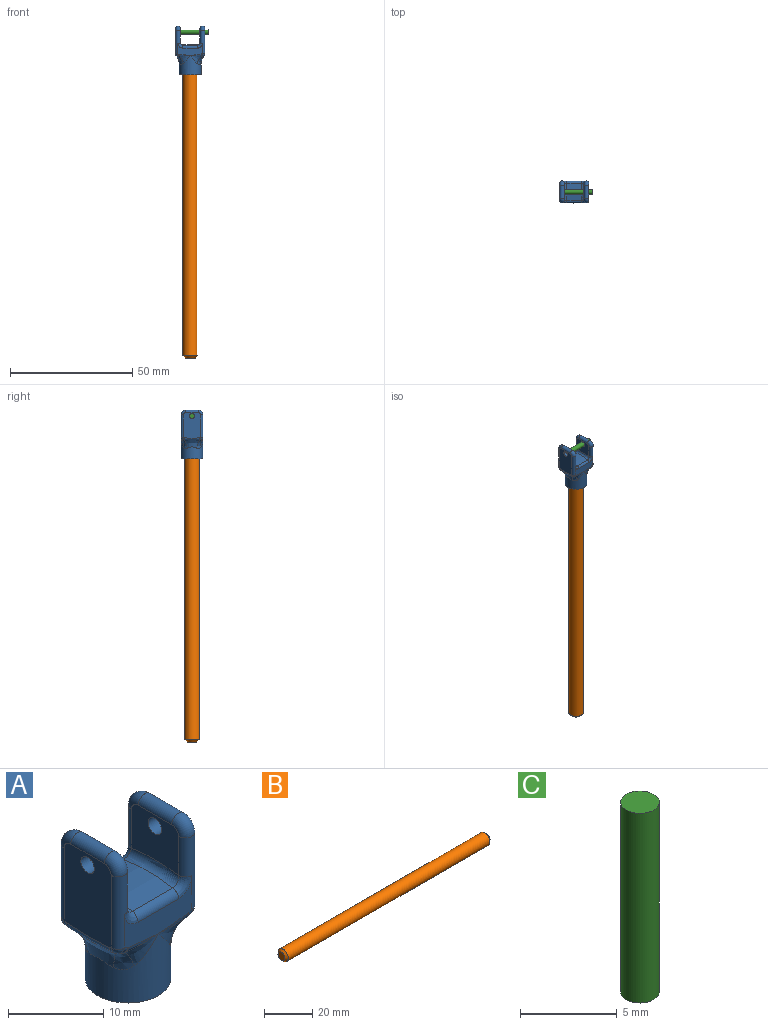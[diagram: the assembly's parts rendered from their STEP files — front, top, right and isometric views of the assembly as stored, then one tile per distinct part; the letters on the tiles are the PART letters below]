
ASSEMBLY  parts=3 mates=1
PART A: 63 faces, bbox 12.4x9.7x20.5 mm
  f0: plane 10.37x5.36mm, normal (0,1,0), area 29.1mm2, adj f12,f14,f38,f39,f40,f41,f42,f43
  f1: plane 10.33x5.33mm, normal (0,-1,0), area 29.1mm2, adj f8,f13,f30,f31,f32,f49,f50,f51
  f2: plane 7x6mm, normal (-1,0,0), area 37.2mm2, adj f8,f9,f10,f11,f12,f28,f54
  f3: cylinder r=4.5mm len=9mm, axis (0,0,-1), area 148.7mm2, adj f18,f19,f20,f21,f22,f23,f24,f25
  f4: plane 7x6mm, normal (1,0,0), area 37.2mm2, adj f13,f14,f15,f16,f17,f29,f57
  f5: plane 10.55x7mm, normal (-1,0,0), area 69.9mm2, adj f13,f14,f15,f16,f17,f29,f34,f35
  f6: plane 10.55x7mm, normal (1,0,0), area 69.9mm2, adj f8,f9,f10,f11,f12,f28,f45,f46
  f7: cylinder r=21.21mm len=7.35mm, axis (-1,0,0), area 44.3mm2, adj f53,f54,f57,f58
  f8: cylinder r=1mm len=9.36mm, axis (0,0,1), area 22.6mm2, adj f1,f2,f6,f9,f48,f56
  f9: torus R=1mm, axis (-1,0,0), area 8.1mm2, adj f2,f6,f8,f10
  f10: cylinder r=1mm len=5mm, axis (0,-1,0), area 15.7mm2, adj f2,f6,f9,f11
  f11: torus R=1mm, axis (-1,0,0), area 8.1mm2, adj f2,f6,f10,f12
  f12: cylinder r=1mm len=9.36mm, axis (0,0,-1), area 22.6mm2, adj f0,f2,f6,f11,f44,f52
  f13: cylinder r=1mm len=9.36mm, axis (0,0,-1), area 22.6mm2, adj f1,f4,f5,f15,f33,f59
  f14: cylinder r=1mm len=9.36mm, axis (0,0,1), area 22.6mm2, adj f0,f4,f5,f16,f37,f55
  f15: torus R=1mm, axis (-1,0,0), area 8.1mm2, adj f4,f5,f13,f17
  f16: torus R=1mm, axis (-1,0,0), area 8.1mm2, adj f4,f5,f14,f17
  f17: cylinder r=1mm len=5mm, axis (0,1,0), area 15.7mm2, adj f4,f5,f15,f16
  f18: bspline ~5.51x3.49mm, area 4.6mm2, adj f3,f19,f41
  f19: bspline ~3.75x3.7mm, area 6.7mm2, adj f3,f18,f20,f42,f43,f45
  f20: bspline ~8.76x3.84mm, area 17mm2, adj f3,f19,f21,f46
  f21: bspline ~3.75x3.6mm, area 6.7mm2, adj f3,f20,f22,f47,f49,f50
  f22: bspline ~5.51x3.49mm, area 4.6mm2, adj f3,f21,f51
  f23: bspline ~5.51x3.49mm, area 4.6mm2, adj f3,f24,f30
  f24: bspline ~3.75x3.7mm, area 6.7mm2, adj f3,f23,f25,f31,f32,f34
  f25: bspline ~8.76x3.84mm, area 17mm2, adj f3,f24,f26,f35
  f26: bspline ~3.75x3.6mm, area 6.7mm2, adj f3,f25,f27,f36,f38,f39
  f27: bspline ~5.51x3.49mm, area 4.6mm2, adj f3,f26,f40
  f28: cylinder r=1mm len=2mm, axis (1,0,0), area 12.6mm2, adj f2,f6
  f29: cylinder r=1mm len=2mm, axis (1,0,0), area 12.6mm2, adj f4,f5
  f30: bspline ~4.78x0.76mm, area 1.2mm2, adj f1,f23,f31
  f31: bspline ~0.8x0.45mm, area 0.1mm2, adj f1,f24,f30,f32
  f32: bspline ~1.15x1.11mm, area 0.7mm2, adj f1,f24,f31,f33
  f33: sphere r=1mm, area 1.1mm2, adj f13,f32,f34
  f34: bspline ~0.98x0.87mm, area 0.5mm2, adj f5,f24,f33,f35
  f35: bspline ~6.85x0.85mm, area 5.5mm2, adj f5,f25,f34,f36
  f36: bspline ~0.97x0.85mm, area 0.5mm2, adj f5,f26,f35,f37
  f37: sphere r=1mm, area 1.1mm2, adj f14,f36,f38
  f38: bspline ~1.2x1.14mm, area 0.7mm2, adj f0,f26,f37,f39
  f39: bspline ~0.79x0.44mm, area 0.1mm2, adj f0,f26,f38,f40
  f40: bspline ~4.9x0.78mm, area 1.2mm2, adj f0,f27,f39
  f41: bspline ~4.69x0.74mm, area 1.2mm2, adj f0,f18,f42
  f42: bspline ~0.8x0.45mm, area 0.1mm2, adj f0,f19,f41,f43
  f43: bspline ~1.31x1.18mm, area 0.7mm2, adj f0,f19,f42,f44
  f44: sphere r=1mm, area 1mm2, adj f12,f43,f45
  f45: bspline ~0.98x0.85mm, area 0.5mm2, adj f6,f19,f44,f46
  f46: bspline ~7.61x0.93mm, area 5.5mm2, adj f6,f20,f45,f47
  f47: bspline ~0.98x0.85mm, area 0.5mm2, adj f6,f21,f46,f48
  f48: sphere r=1mm, area 1mm2, adj f8,f47,f49
  f49: bspline ~1.2x1.14mm, area 0.7mm2, adj f1,f21,f48,f50
  f50: bspline ~0.8x0.44mm, area 0.1mm2, adj f1,f21,f49,f51
  f51: bspline ~4.69x0.74mm, area 1.2mm2, adj f1,f22,f50
  f52: bspline ~2.44x2.36mm, area 3.2mm2, adj f0,f12,f53,f54
  f53: cylinder r=1mm len=6mm, axis (-1,0,0), area 8.4mm2, adj f0,f7,f52,f55
  f54: torus R=22.21mm, axis (-1,0,0), area 11.3mm2, adj f2,f7,f52,f56
  f55: bspline ~2.49x2.36mm, area 3.2mm2, adj f0,f14,f53,f57
  f56: bspline ~2.49x2.36mm, area 3.2mm2, adj f1,f8,f54,f58
  f57: torus R=22.21mm, axis (-1,0,0), area 11.3mm2, adj f4,f7,f55,f59
  f58: cylinder r=1mm len=6mm, axis (-1,0,0), area 8.4mm2, adj f1,f7,f56,f59
  f59: bspline ~2.44x2.36mm, area 3.2mm2, adj f1,f13,f57,f58
  f60: plane 9x9mm, normal (0,0,-1), area 32.9mm2, adj f3,f62
  f61: plane 6.25x6.25mm, normal (0,0,-1), area 30.7mm2, adj f62
  f62: cylinder r=3.12mm len=8mm, axis (0,0,-1), area 157.1mm2, adj f60,f61
PART B: 5 faces, bbox 120x6x6 mm
  f0: cylinder r=3mm len=118mm, axis (-1,0,0), area 2224.2mm2, adj f3,f4
  f1: plane 4x4mm, normal (1,0,0), area 12.6mm2, adj f4
  f2: plane 4x4mm, normal (-1,0,0), area 12.6mm2, adj f3
  f3: cone r=3mm half-angle=45deg, axis (1,0,0), area 22.2mm2, adj f0,f2
  f4: cone r=2mm half-angle=45deg, axis (-1,0,0), area 22.2mm2, adj f0,f1
PART C: 3 faces, bbox 2x2x12 mm
  f0: cylinder r=1mm len=12mm, axis (0,0,-1), area 75.4mm2, adj f1,f2
  f1: plane 2x2mm, normal (0,0,1), area 3.1mm2, adj f0
  f2: plane 2x2mm, normal (0,0,-1), area 3.1mm2, adj f0
PLACE A t=(93.04,132.09,72.22)mm
PLACE B rot(axis=(0,1,0),90deg) t=(-50.3,-11.53,12.22)mm
PLACE C rot(axis=(0,1,0),90deg) t=(19.8,174.73,-26.95)mm
MATE fastened C.f0 <-> A.f28  axis (1,0,0) through (31.8,67.51,85.79)mm
